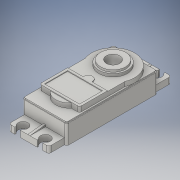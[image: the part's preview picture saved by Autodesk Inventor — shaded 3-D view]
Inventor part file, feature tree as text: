
AUTODESK INVENTOR PART (.ipt)
format: ipt  version: 2016 (Build 200138000, 138)  size: 295,936 bytes
history: native  units: mm
features: sketch x13, extrude x12, mirror x2, fillet x2, other x1
ambient origin geometry x8: Origin, YZ Plane, XZ Plane, XY Plane, X Axis, Y Axis, Z Axis, Center Point
bodies: Body1 (feature_tree)
feature tree (30):
  other  "Sólido1"
  extrude  "Extrusión1"  Depth=40.6mm
  extrude  "Extrusión2"  Depth=9.0mm
  extrude  "Extrusión5"  Depth=9.0mm TaperAngle=0.0deg
  extrude  "Extrusión6"  Depth=2.8mm TaperAngle=0.0deg
  extrude  "Extrusión7"  Depth=2.8mm TaperAngle=0.0deg
  mirror  "Simetría3"
  mirror  "Simetría4"
  extrude  "Extrusión8"  Depth=1.0mm TaperAngle=0.0deg
  extrude  "Extrusión9"  Depth=9.6mm
  extrude  "Extrusión10"  Depth=2.0mm TaperAngle=0.0deg
  extrude  "Extrusión11"  Depth=9.4mm
  extrude  "Extrusión12"  Depth=2.0mm
  extrude  "Extrusión13"  Depth=1.3mm
  extrude  "Extrusión14"  Depth=17.8mm
  fillet  "Empalme1"  Radius=12.5mm
  fillet  "Empalme2"  Radius=1.1mm
  sketch  "Boceto18"  dims[d64=0.3mm d65=0.0mm d66=3.88mm d67=1.44mm d68=0.3mm d69=0.0mm d70=0.3mm d71=0.5mm d72=0.0mm d73=1.0mm d74=0.7mm]
  sketch  "Boceto1"  dims[d0=19.8mm d1=40.6mm]
  sketch  "Boceto2"  dims[d2=9.0mm d3=0.0mm d4=6.0mm]
  sketch  "Boceto5"  dims[d5=10.0mm d6=9.0mm d7=0.0mm]
  sketch  "Boceto6"  dims[d23=17.8mm d24=7.0mm d25=2.8mm d26=0.0mm]
  sketch  "Boceto8"  dims[d27=4.4mm d28=2.41mm d29=5.0mm d30=2.65mm d31=0.6mm d32=2.8mm d33=0.0mm]
  sketch  "Boceto9"  dims[d34=0.8mm d35=1.0mm d36=0.0mm]
  sketch  "Boceto11"  dims[d37=19.2mm d40=9.6mm]
  sketch  "Boceto12"  dims[d42=20.3mm d43=2.0mm d44=0.0mm]
  sketch  "Boceto13"  dims[d50=2.2mm d51=9.4mm]
  sketch  "Boceto15"  dims[d52=2.0mm d53=0.0mm d54=12.8mm]
  sketch  "Boceto16"  dims[d55=1.3mm d56=0.0mm d57=11.2mm]
  sketch  "Boceto17"  dims[d58=0.9mm d59=0.0mm d61=17.8mm d62=12.5mm d63=1.1mm]
